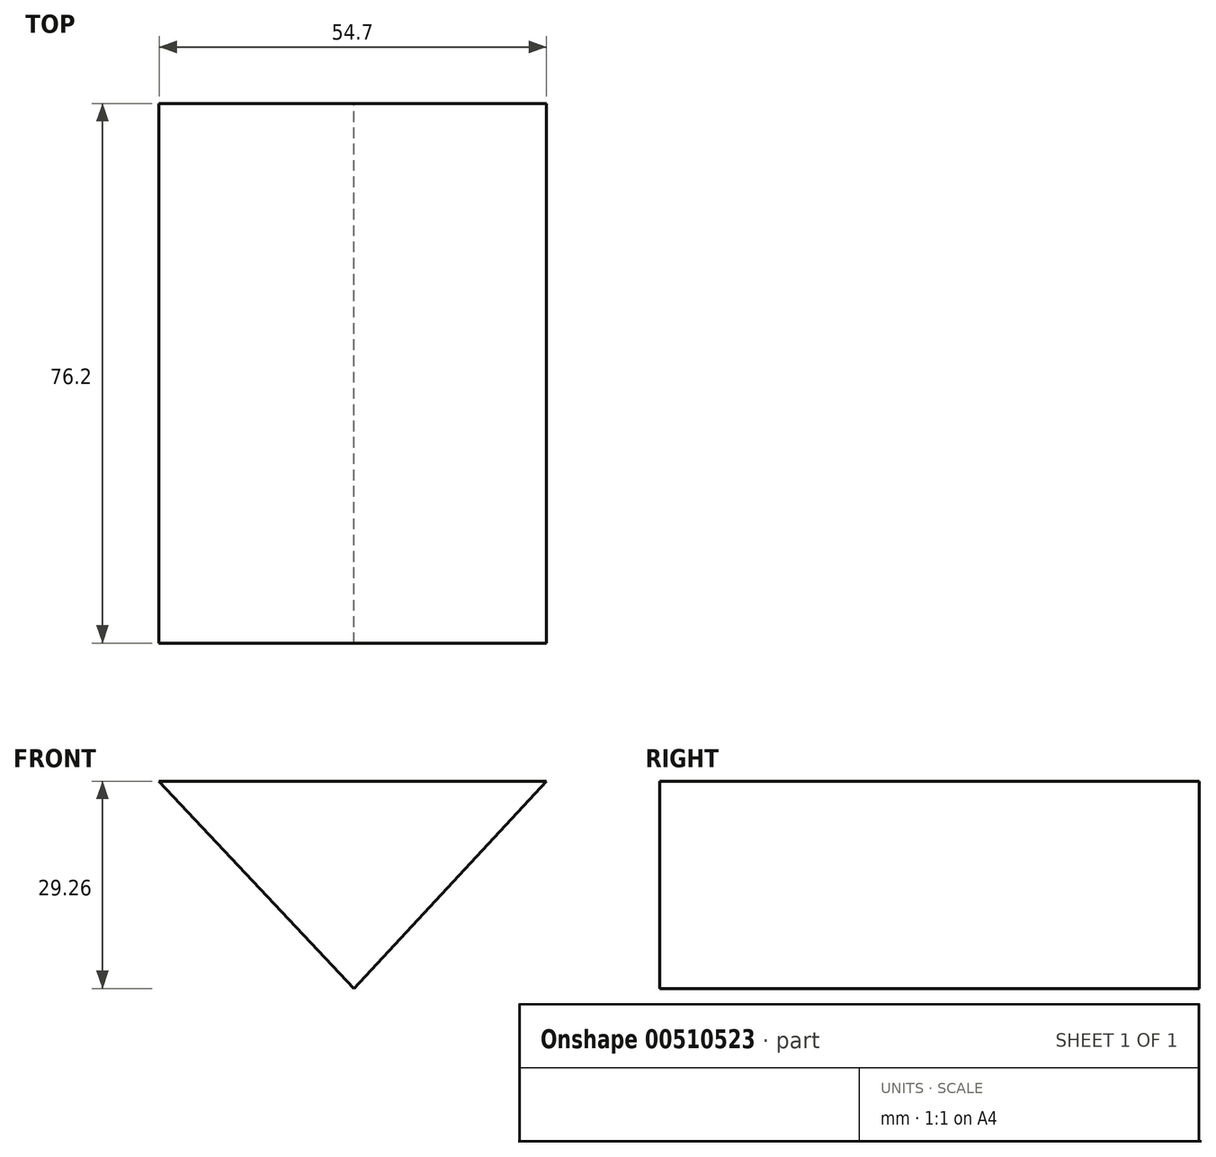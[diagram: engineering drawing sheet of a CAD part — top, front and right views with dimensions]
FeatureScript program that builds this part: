
annotation { "Feature Type Name" : "Feature", "Feature Type Description" : "" }
export const myFeature = defineFeature(function(context is Context, id is Id, definition is map)
    precondition{}
    {
        {
            var Q0;
            Q0=qCreatedBy(makeId("Front.planeOp"),FACE);
            var sketch = newSketch(context, id + "F0", { "sketchPlane" : qUnion([Q0])});
            skLineSegment(sketch, "E0", {"start": v(-27.5, 18.52) * mm, "end": v(27.2, 18.52) * mm});
            skLineSegment(sketch, "E1", {"start": v(27.2, 18.52) * mm, "end": v(0, -10.74) * mm});
            skLineSegment(sketch, "E2", {"start": v(0, -10.74) * mm, "end": v(-27.5, 18.52) * mm});
            skSolve(sketch);
        }
        {
            var Q0;
            Q0 = qSketchRegion(id + "F0", true);
            extrude(context, id + "F1", {"entities" : qUnion([Q0]), "depth" : 76.2 * mm});
        }
    });
